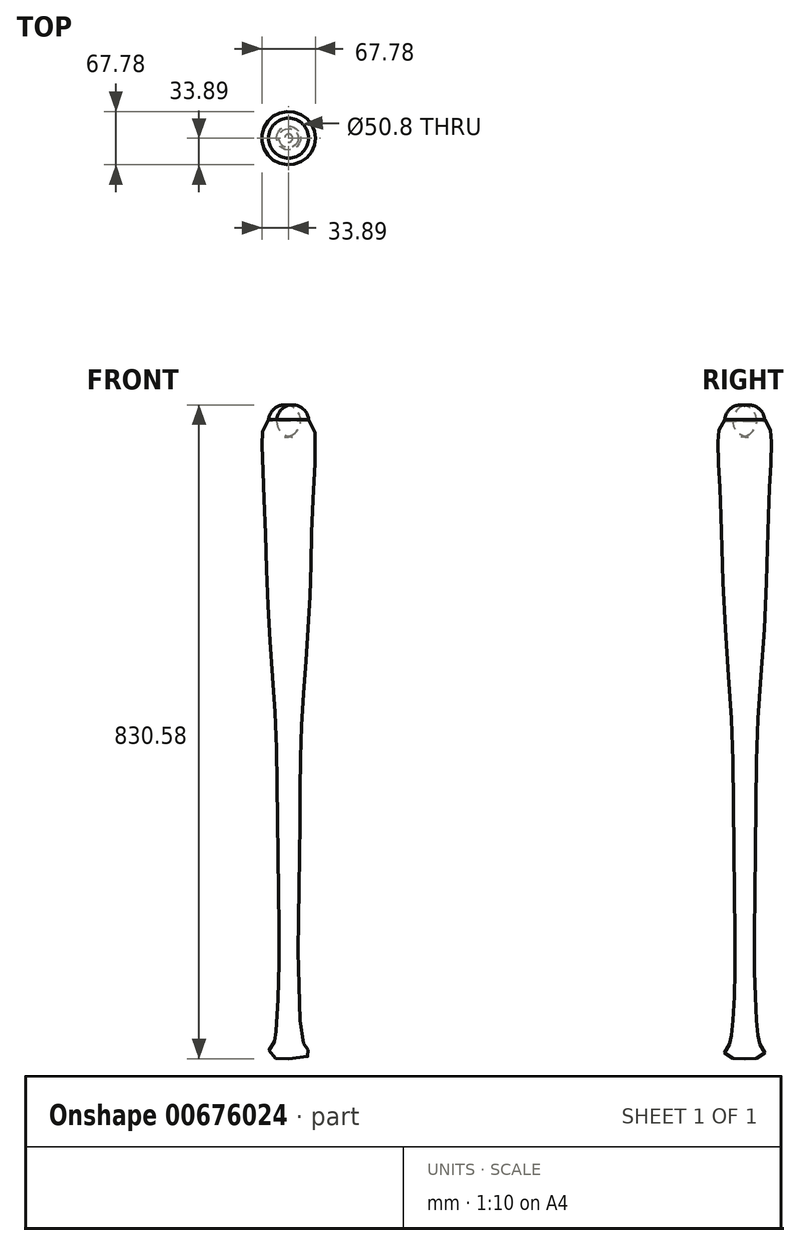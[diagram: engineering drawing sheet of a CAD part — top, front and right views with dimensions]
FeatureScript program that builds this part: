
annotation { "Feature Type Name" : "Feature", "Feature Type Description" : "" }
export const myFeature = defineFeature(function(context is Context, id is Id, definition is map)
    precondition{}
    {
        {
            var Q0;
            Q0=qCreatedBy(makeId("Front.planeOp"),FACE);
            var sketch = newSketch(context, id + "F0", { "sketchPlane" : qUnion([Q0])});
            skFitSpline(sketch, "E0", {"points": [v(0, 0) * mm, v(24.95, 4.27) * mm, v(25.4, 8.88) * mm, v(22.73, 14.12) * mm, v(19.05, 19.05) * mm, v(12.7, 101.6) * mm, v(12.7, 203.2) * mm, v(14.29, 304.8) * mm, v(15.88, 406.4) * mm, v(22.23, 508) * mm, v(27.79, 609.6) * mm, v(30.96, 711.2) * mm, v(31.75, 804.42) * mm, v(0, 812.8) * mm], "startDerivative": vector(1235.4, 0) * mm, "endDerivative": vector(-1213.33, -5.02) * mm});
            skLineSegment(sketch, "E1", {"start": v(0, 0) * mm, "end": v(0, 812.8) * mm, "construction": true});
            skLineSegment(sketch, "E2", {"start": v(0, 812.8) * mm, "end": v(0, 0) * mm});
            skSolve(sketch);
        }
        {
            var Q0;
            Q0=qSketchRegion(id+"F0",true);
            var Q1;
            Q1=sQuery(id+"F0.wireOp",EDGE,"E2");
            revolve(context, id + "F1", {"entities" : qUnion([Q0]), "axis" : qUnion([Q1]), "revolveType" : RevolveType.FULL});
        }
        {
            var Q0;
            Q0=qCreatedBy(makeId("Top.planeOp"),FACE);
            cPlane(context, id + "F2", {"entities" : qUnion([Q0]), "cplaneType" : CPlaneType.OFFSET, "offset" : 815.34 * mm, "width" : 152.4 * mm, "height" : 152.4 * mm});
        }
        {
            var Q0;
            Q0=qCreatedBy(id+"F2.planeOp",FACE);
            var sketch = newSketch(context, id + "F3", { "sketchPlane" : qUnion([Q0])});
            skCircle(sketch, "E3", {"center": v(0, 0) * mm, "radius": 25.4 * mm});
            skSolve(sketch);
        }
        {
            var Q0;
            Q0=qSketchRegion(id+"F3",true);
            extrude(context, id + "F4", {"entities" : qUnion([Q0]), "operationType" : NewBodyOperationType.REMOVE, "oppositeDirection" : true, "depth" : 25.4 * mm});
        }
        {
            var Q0;
            Q0=makeQuery(id+"F4.boolean.opBoolean","COPY",EDGE,{"derivedFrom":makeQuery(id+"F4.opExtrude","CAP_EDGE",EDGE,{"disambiguationData":[OSD([sQuery(id+"F3.wireOp",EDGE,"E3")])],"isStart":false})});
            fillet(context, id + "F5", {"entities" : qUnion([Q0]), "radius" : 20.32 * mm, "tangentPropagation" : true, "allowEdgeOverflow" : false});
        }
    });
